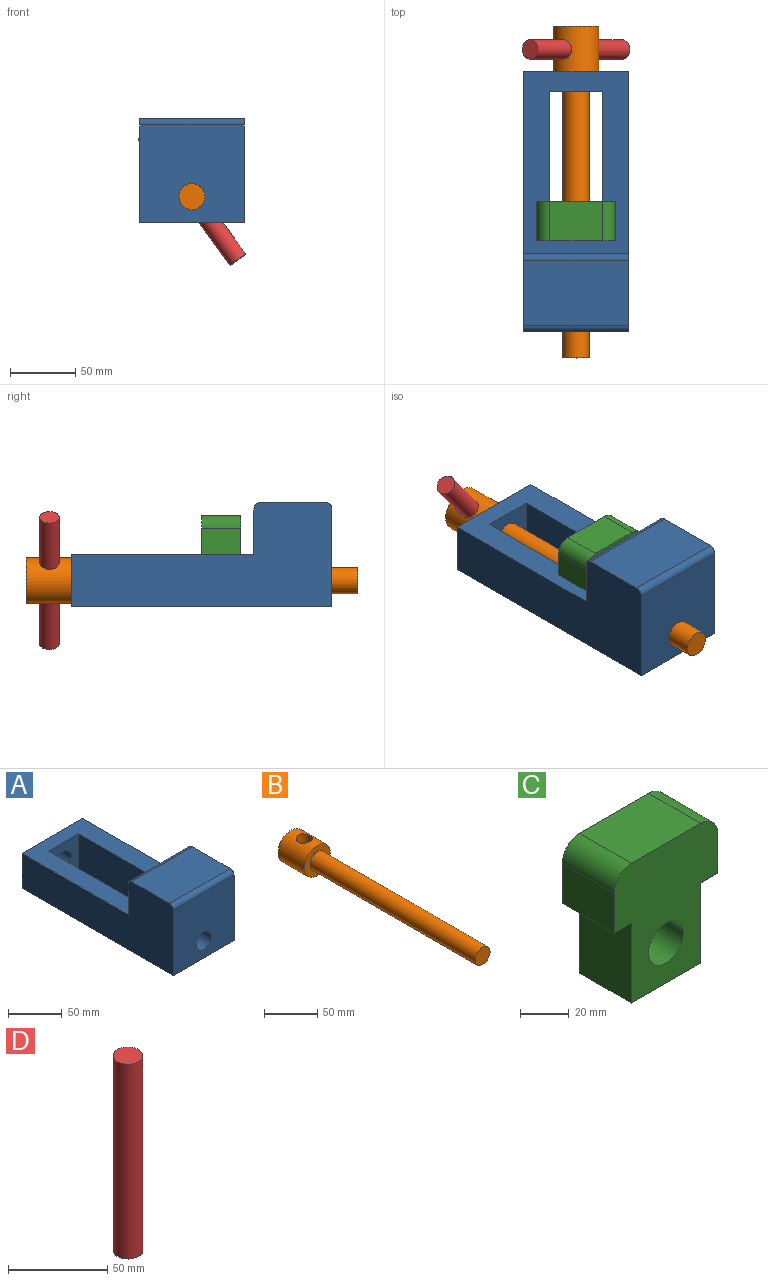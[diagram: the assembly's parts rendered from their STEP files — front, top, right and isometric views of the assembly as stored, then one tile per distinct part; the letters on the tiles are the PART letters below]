
ASSEMBLY  parts=4 mates=4
PART A: 16 faces, bbox 80x200x80 mm
  f0: cylinder r=5mm len=80mm, axis (-1,0,0), area 628.3mm2, adj f1,f7,f8,f9
  f1: plane 80x50mm, normal (0,0,1), area 4000mm2, adj f0,f2,f8,f9
  f2: cylinder r=5mm len=80mm, axis (-1,0,0), area 628.3mm2, adj f1,f3,f8,f9
  f3: plane 80x75mm, normal (0,-1,0), area 5685.8mm2, adj f2,f4,f8,f9,f14
  f4: plane 200x80mm, normal (0,0,-1), area 11400mm2, adj f3,f5,f8,f9,f10,f11,f12,f13
  f5: plane 80x40mm, normal (0,1,0), area 2885.8mm2, adj f4,f6,f8,f9,f15
  f6: plane 140x80mm, normal (0,0,1), area 6600mm2, adj f5,f7,f8,f9,f10,f11,f12,f13
  f7: plane 80x35mm, normal (0,1,0), area 2800mm2, adj f0,f6,f8,f9
  f8: plane 200x80mm, normal (1,0,0), area 10389.3mm2, adj f0,f1,f2,f3,f4,f5,f6,f7
  f9: plane 200x80mm, normal (-1,0,0), area 10389.3mm2, adj f0,f1,f2,f3,f4,f5,f6,f7
  f10: plane 40x40mm, normal (0,-1,0), area 1285.8mm2, adj f4,f6,f11,f12,f15
  f11: plane 115x40mm, normal (-1,0,0), area 4600mm2, adj f4,f6,f10,f13
  f12: plane 115x40mm, normal (1,0,0), area 4600mm2, adj f4,f6,f10,f13
  f13: plane 40x40mm, normal (0,1,0), area 1285.8mm2, adj f4,f6,f11,f12,f14
  f14: cylinder r=10mm len=70mm, axis (0,1,0), area 4398.2mm2, adj f3,f13
  f15: cylinder r=10mm len=20mm, axis (0,1,0), area 942.5mm2, adj f5,f10
PART B: 6 faces, bbox 35x255x35 mm
  f0: cylinder r=17.5mm len=35mm, axis (0,-1,0), area 3486.7mm2, adj f1,f2,f5
  f1: plane 35x35mm, normal (0,1,0), area 962.1mm2, adj f0
  f2: plane 35x35mm, normal (0,-1,0), area 648mm2, adj f0,f3
  f3: cylinder r=10mm len=220mm, axis (0,1,0), area 13823mm2, adj f2,f4
  f4: plane 20x20mm, normal (0,-1,0), area 314.2mm2, adj f3
  f5: cylinder r=7.5mm len=35mm, axis (0,0,1), area 1570.7mm2, adj f0
PART C: 13 faces, bbox 60x30x70 mm
  f0: cylinder r=10mm len=30mm, axis (0,1,0), area 471.2mm2, adj f1,f10,f11,f12
  f1: plane 30x20mm, normal (-1,0,0), area 600mm2, adj f0,f2,f11,f12
  f2: plane 30x10mm, normal (0,0,-1), area 300mm2, adj f1,f3,f11,f12
  f3: plane 40x30mm, normal (-1,0,0), area 1200mm2, adj f2,f4,f11,f12
  f4: plane 40x30mm, normal (0,0,-1), area 1200mm2, adj f3,f5,f11,f12
  f5: plane 40x30mm, normal (1,0,0), area 1200mm2, adj f4,f6,f11,f12
  f6: plane 30x10mm, normal (0,0,-1), area 300mm2, adj f5,f7,f11,f12
  f7: plane 30x20mm, normal (1,0,0), area 600mm2, adj f6,f8,f11,f12
  f8: cylinder r=10mm len=30mm, axis (0,1,0), area 471.2mm2, adj f7,f10,f11,f12
  f9: cylinder r=10mm len=30mm, axis (0,1,0), area 1885mm2, adj f11,f12
  f10: plane 40x30mm, normal (0,0,1), area 1200mm2, adj f0,f8,f11,f12
  f11: plane 70x60mm, normal (0,-1,0), area 3042.9mm2, adj f0,f1,f2,f3,f4,f5,f6,f7
  f12: plane 70x60mm, normal (0,1,0), area 3042.9mm2, adj f0,f1,f2,f3,f4,f5,f6,f7
PART D: 3 faces, bbox 15x15x120 mm
  f0: cylinder r=7.5mm len=120mm, axis (0,0,-1), area 5654.9mm2, adj f1,f2
  f1: plane 15x15mm, normal (0,0,1), area 176.7mm2, adj f0
  f2: plane 15x15mm, normal (0,0,-1), area 176.7mm2, adj f0
PLACE A t=(-63.88,-30.52,22.17)mm fixed
PLACE B rot(axis=(0,-1,0),36deg) t=(-52.12,-30.52,25.99)mm
PLACE C t=(-63.88,-45.52,22.17)mm
PLACE D rot(axis=(0.29,-0.38,-0.88),80.8deg) t=(-142.93,53.47,-39.99)mm
MATE revolute B.f0 <-> A.f14  axis (0,-1,0) through (-63.88,69.48,42.17)mm
MATE revolute B.f5 <-> D.f0  axis (-0.59,0,0.81) through (-63.88,86.48,42.17)mm
MATE slider C.f9 <-> A.f14  axis (0,1,0) through (-63.88,-60.52,42.17)mm
MATE cylindrical B.f0 <-> C.f9  axis (0,1,0) through (-63.88,-40.52,42.17)mm
